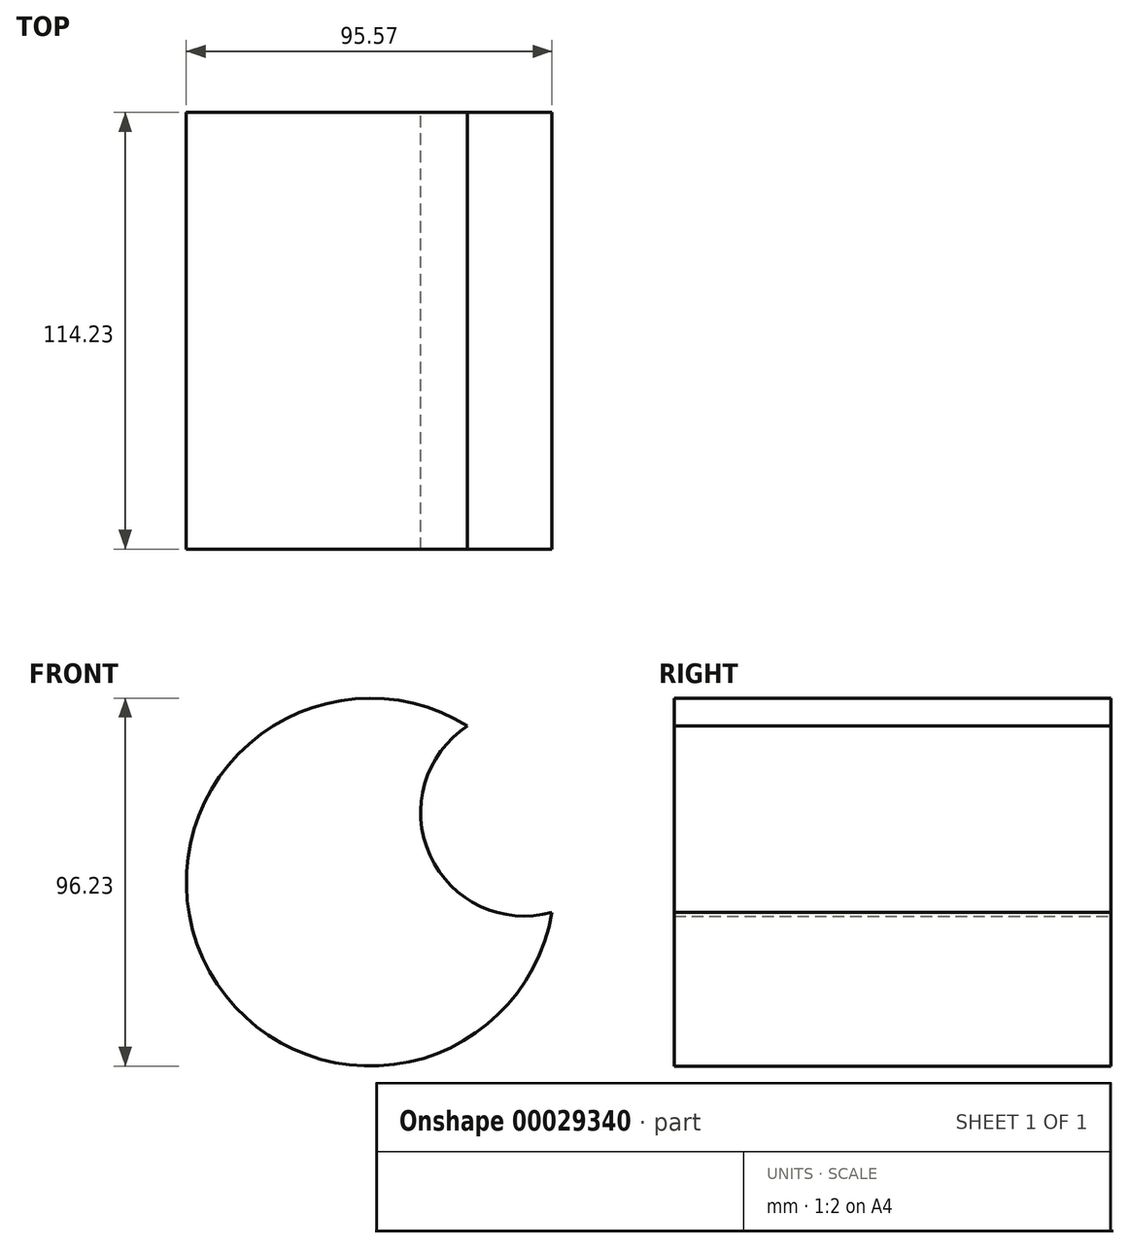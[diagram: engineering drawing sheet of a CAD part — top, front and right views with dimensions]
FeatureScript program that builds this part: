
annotation { "Feature Type Name" : "Feature", "Feature Type Description" : "" }
export const myFeature = defineFeature(function(context is Context, id is Id, definition is map)
    precondition{}
    {
        {
            var Q0;
            Q0=qCreatedBy(makeId("Front.planeOp"),FACE);
            var sketch = newSketch(context, id + "F0", { "sketchPlane" : qUnion([Q0])});
            skCircle(sketch, "E0", {"center": v(0, 25.67) * mm, "radius": 48.11 * mm});
            skSolve(sketch);
        }
        {
            var Q0;
            Q0=makeQuery(id+"F0.imprint","IMPRINT",FACE,{"disambiguationData":[TD([[makeQuery(id+"F0.imprint","IMPRINT",EDGE,{"derivedFrom":sQuery(id+"F0.wireOp",EDGE,"E0")}),1.0]])]});
            var sketch = newSketch(context, id + "F1", { "sketchPlane" : qUnion([Q0])});
            skCircle(sketch, "E1", {"center": v(40.26, 43.87) * mm, "radius": 27.1 * mm});
            skSolve(sketch);
        }
        {
            var Q0;
            {var subQ0=makeQuery(id+"F0.imprint","IMPRINT",EDGE,{"derivedFrom":sQuery(id+"F0.wireOp",EDGE,"E0")});var subQ1=sQuery(id+"F1.wireOp",EDGE,"E1");var subQ3=makeQuery(id+"F1.imprint","INTERSECT",VERTEX,{"disambiguationData":[OD(0.0)],"derivedFrom":[subQ0,subQ1]});Q0=makeQuery(id+"F1.imprint","IMPRINT",FACE,{"disambiguationData":[TD([[makeQuery(id+"F1.imprint","IMPRINT",EDGE,{"disambiguationData":[TD([[subQ3,-1.0]])],"derivedFrom":subQ1}),-1.0]])]});}
            extrude(context, id + "F2", {"entities" : qUnion([Q0]), "depth" : 114.23 * mm});
        }
    });
